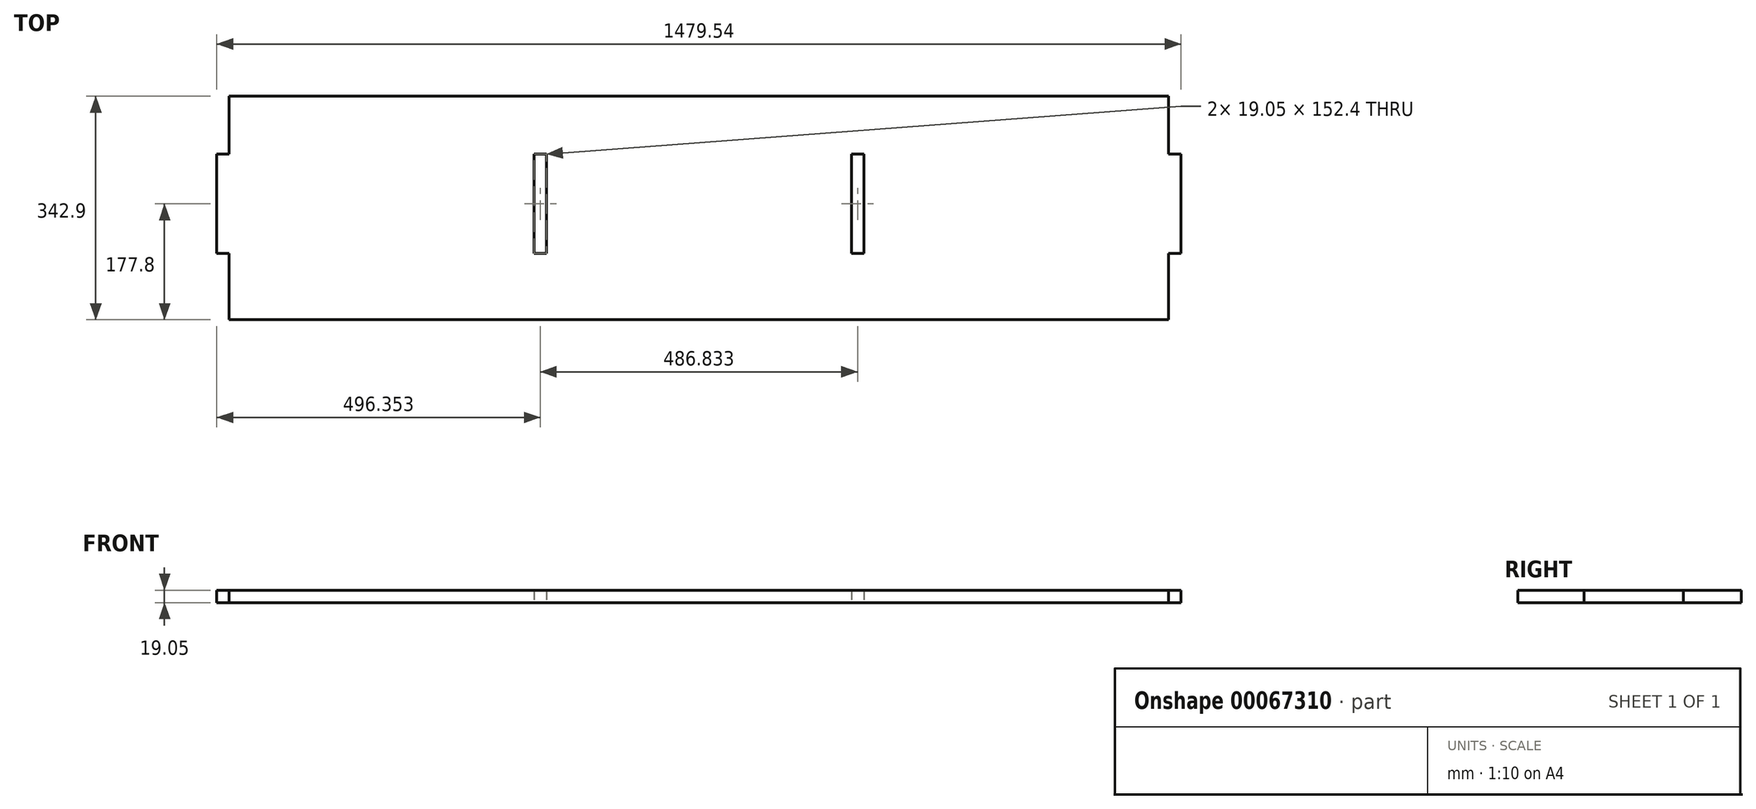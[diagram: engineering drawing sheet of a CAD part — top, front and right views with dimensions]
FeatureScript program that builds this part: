
annotation { "Feature Type Name" : "Feature", "Feature Type Description" : "" }
export const myFeature = defineFeature(function(context is Context, id is Id, definition is map)
    precondition{}
    {
        {
            var Q0;
            Q0=qCreatedBy(makeId("Top.planeOp"),FACE);
            var sketch = newSketch(context, id + "F0", { "sketchPlane" : qUnion([Q0])});
            skLineSegment(sketch, "E0.bottom", {"start": v(-720.73, 0) * mm, "end": v(720.73, 0) * mm});
            skLineSegment(sketch, "E0.top", {"start": v(-720.73, -342.9) * mm, "end": v(720.73, -342.9) * mm});
            skLineSegment(sketch, "E0.left", {"start": v(-720.73, 0) * mm, "end": v(-720.73, -342.9) * mm});
            skLineSegment(sketch, "E0.right", {"start": v(720.73, 0) * mm, "end": v(720.73, -342.9) * mm});
            skLineSegment(sketch, "E1.bottom", {"start": v(-720.73, -88.9) * mm, "end": v(-739.77, -88.9) * mm});
            skLineSegment(sketch, "E1.top", {"start": v(-720.73, -241.3) * mm, "end": v(-739.78, -241.3) * mm});
            skLineSegment(sketch, "E1.left", {"start": v(-720.73, -88.9) * mm, "end": v(-720.73, -241.3) * mm});
            skLineSegment(sketch, "E1.right", {"start": v(-739.77, -88.9) * mm, "end": v(-739.78, -241.3) * mm});
            skLineSegment(sketch, "E2.bottom", {"start": v(720.73, -88.9) * mm, "end": v(739.78, -88.9) * mm});
            skLineSegment(sketch, "E2.top", {"start": v(720.73, -241.3) * mm, "end": v(739.78, -241.3) * mm});
            skLineSegment(sketch, "E2.left", {"start": v(720.73, -88.9) * mm, "end": v(720.73, -241.3) * mm});
            skLineSegment(sketch, "E2.right", {"start": v(739.78, -88.9) * mm, "end": v(739.78, -241.3) * mm});
            skLineSegment(sketch, "E3.bottom", {"start": v(-441.33, 0) * mm, "end": v(-288.93, 0) * mm});
            skLineSegment(sketch, "E3.top", {"start": v(-441.33, 19.05) * mm, "end": v(-288.93, 19.05) * mm});
            skLineSegment(sketch, "E3.left", {"start": v(-441.33, 0) * mm, "end": v(-441.33, 19.05) * mm});
            skLineSegment(sketch, "E3.right", {"start": v(-288.93, 0) * mm, "end": v(-288.93, 19.05) * mm});
            skLineSegment(sketch, "E4.bottom", {"start": v(288.93, 0) * mm, "end": v(441.33, 0) * mm});
            skLineSegment(sketch, "E4.top", {"start": v(288.93, 19.05) * mm, "end": v(441.32, 19.05) * mm});
            skLineSegment(sketch, "E4.left", {"start": v(288.93, 0) * mm, "end": v(288.93, 19.05) * mm});
            skLineSegment(sketch, "E4.right", {"start": v(441.33, 0) * mm, "end": v(441.33, 19.05) * mm});
            skLineSegment(sketch, "E5.bottom", {"start": v(-252.94, -88.9) * mm, "end": v(-233.9, -88.9) * mm});
            skLineSegment(sketch, "E5.top", {"start": v(-252.94, -241.3) * mm, "end": v(-233.9, -241.3) * mm});
            skLineSegment(sketch, "E5.left", {"start": v(-252.94, -88.9) * mm, "end": v(-252.94, -241.3) * mm});
            skLineSegment(sketch, "E5.right", {"start": v(-233.9, -88.9) * mm, "end": v(-233.9, -241.3) * mm});
            skLineSegment(sketch, "E6.bottom", {"start": v(233.9, -88.9) * mm, "end": v(252.94, -88.9) * mm});
            skLineSegment(sketch, "E6.top", {"start": v(233.9, -241.3) * mm, "end": v(252.94, -241.3) * mm});
            skLineSegment(sketch, "E6.left", {"start": v(233.9, -88.9) * mm, "end": v(233.9, -241.3) * mm});
            skLineSegment(sketch, "E6.right", {"start": v(252.94, -88.9) * mm, "end": v(252.94, -241.3) * mm});
            skSolve(sketch);
        }
        {
            var Q0;
            {var subQ2=sQuery(id+"F0.wireOp",EDGE,"E0.top");Q0=makeQuery(id+"F0.imprint","IMPRINT",FACE,{"disambiguationData":[TD([[makeQuery(id+"F0.imprint","IMPRINT",EDGE,{"derivedFrom":subQ2}),1.0]])]});}
            var Q1;
            Q1=makeQuery(id+"F0.imprint","IMPRINT",FACE,{"disambiguationData":[TD([[makeQuery(id+"F0.imprint","IMPRINT",EDGE,{"derivedFrom":sQuery(id+"F0.wireOp",EDGE,"E3.bottom")}),1.0]])]});
            var Q2;
            Q2=makeQuery(id+"F0.imprint","IMPRINT",FACE,{"disambiguationData":[TD([[makeQuery(id+"F0.imprint","IMPRINT",EDGE,{"derivedFrom":sQuery(id+"F0.wireOp",EDGE,"E4.bottom")}),1.0]])]});
            var Q3;
            Q3=makeQuery(id+"F0.imprint","IMPRINT",FACE,{"disambiguationData":[TD([[makeQuery(id+"F0.imprint","IMPRINT",EDGE,{"derivedFrom":sQuery(id+"F0.wireOp",EDGE,"E2.bottom")}),-1.0]])]});
            var Q4;
            Q4=makeQuery(id+"F0.imprint","IMPRINT",FACE,{"disambiguationData":[TD([[makeQuery(id+"F0.imprint","IMPRINT",EDGE,{"derivedFrom":sQuery(id+"F0.wireOp",EDGE,"E1.bottom")}),1.0]])]});
            extrude(context, id + "F1", {"entities" : qUnion([Q0, Q1, Q2, Q3, Q4]), "depth" : 19.05 * mm});
        }
    });
